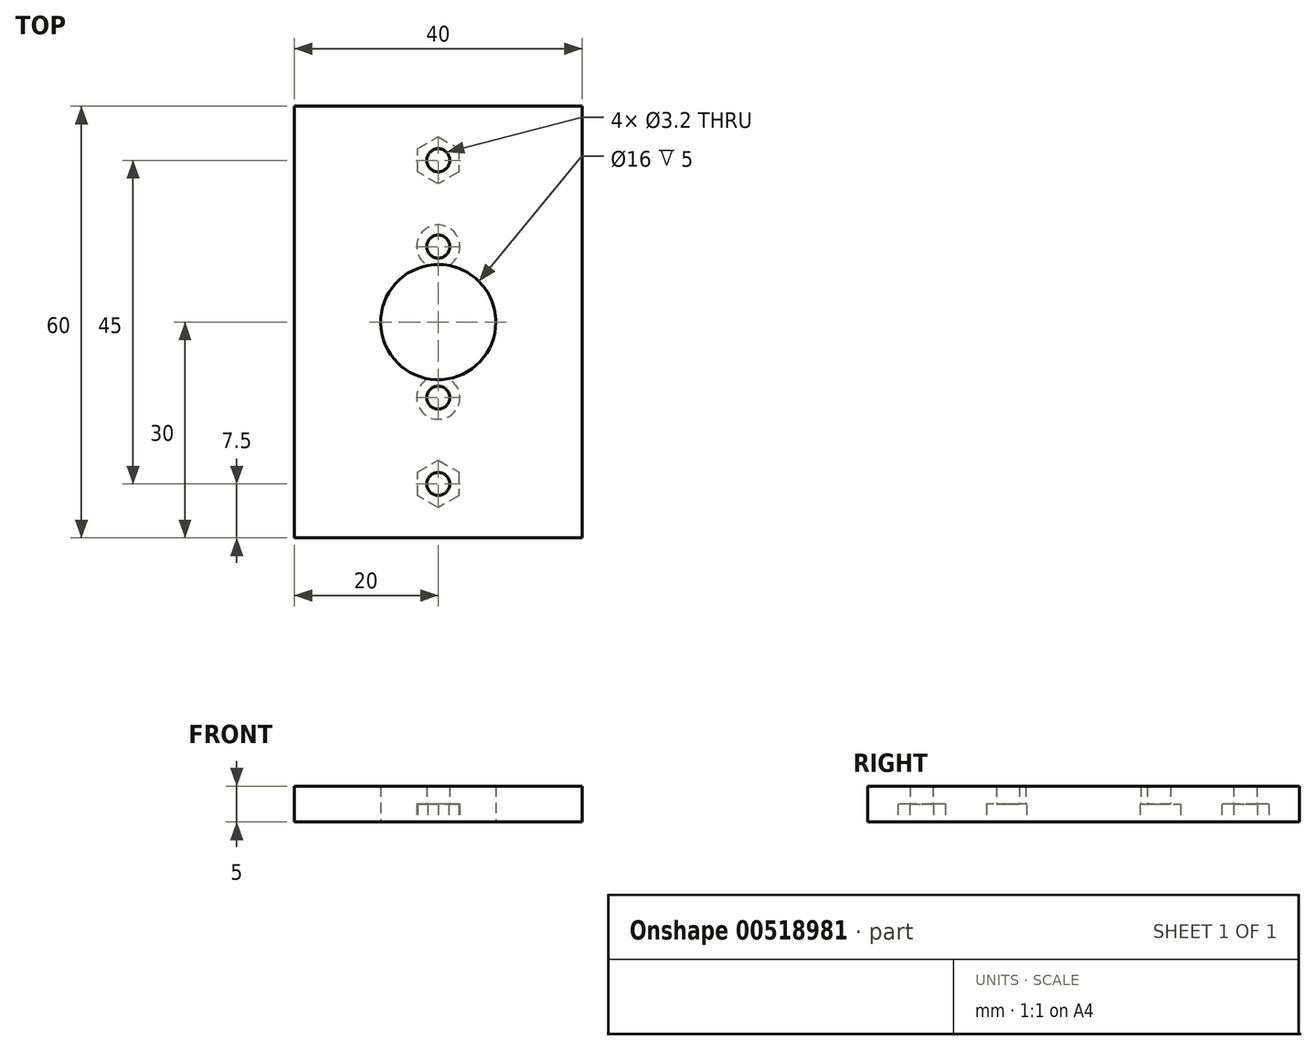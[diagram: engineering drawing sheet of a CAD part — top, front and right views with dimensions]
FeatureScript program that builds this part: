
annotation { "Feature Type Name" : "Feature", "Feature Type Description" : "" }
export const myFeature = defineFeature(function(context is Context, id is Id, definition is map)
    precondition{}
    {
        {
            var Q0;
            Q0=qCreatedBy(makeId("Top.planeOp"),FACE);
            var sketch = newSketch(context, id + "F0", { "sketchPlane" : qUnion([Q0])});
            skLineSegment(sketch, "E0.bottom", {"start": v(-20, 30) * mm, "end": v(20, 30) * mm});
            skLineSegment(sketch, "E0.top", {"start": v(-20, -30) * mm, "end": v(20, -30) * mm});
            skLineSegment(sketch, "E0.left", {"start": v(-20, 30) * mm, "end": v(-20, -30) * mm});
            skLineSegment(sketch, "E0.right", {"start": v(20, 30) * mm, "end": v(20, -30) * mm});
            skCircle(sketch, "E1.cCircle", {"center": v(0, 22.5) * mm, "radius": 2.85 * mm, "construction": true});
            skLineSegment(sketch, "E1.0", {"start": v(2.85, 20.85) * mm, "end": v(0, 19.2) * mm});
            skLineSegment(sketch, "E1.1", {"start": v(0, 19.2) * mm, "end": v(-2.85, 20.85) * mm});
            skLineSegment(sketch, "E1.2", {"start": v(-2.85, 20.85) * mm, "end": v(-2.85, 24.15) * mm});
            skLineSegment(sketch, "E1.3", {"start": v(-2.85, 24.15) * mm, "end": v(0, 25.8) * mm});
            skLineSegment(sketch, "E1.4", {"start": v(0, 25.8) * mm, "end": v(2.85, 24.15) * mm});
            skLineSegment(sketch, "E1.5", {"start": v(2.85, 24.15) * mm, "end": v(2.85, 20.85) * mm});
            skPoint(sketch, "E1.0.midPoint", {"position": v(1.43, 20.03) * mm});
            skCircle(sketch, "E2.cCircle", {"center": v(0, -22.5) * mm, "radius": 2.85 * mm, "construction": true});
            skLineSegment(sketch, "E2.0", {"start": v(2.85, -24.15) * mm, "end": v(0, -25.8) * mm});
            skLineSegment(sketch, "E2.1", {"start": v(0, -25.8) * mm, "end": v(-2.85, -24.15) * mm});
            skLineSegment(sketch, "E2.2", {"start": v(-2.85, -24.15) * mm, "end": v(-2.85, -20.85) * mm});
            skLineSegment(sketch, "E2.3", {"start": v(-2.85, -20.85) * mm, "end": v(0, -19.2) * mm});
            skLineSegment(sketch, "E2.4", {"start": v(0, -19.2) * mm, "end": v(2.85, -20.85) * mm});
            skLineSegment(sketch, "E2.5", {"start": v(2.85, -20.85) * mm, "end": v(2.85, -24.15) * mm});
            skPoint(sketch, "E2.0.midPoint", {"position": v(1.43, -24.97) * mm});
            skCircle(sketch, "E3", {"center": v(0, 22.5) * mm, "radius": 1.6 * mm});
            skCircle(sketch, "E4", {"center": v(0, -22.5) * mm, "radius": 1.6 * mm});
            skLineSegment(sketch, "E5", {"start": v(-20, 30) * mm, "end": v(20, -30) * mm, "construction": true});
            skCircle(sketch, "E6", {"center": v(0, 0) * mm, "radius": 8 * mm});
            skLineSegment(sketch, "E7", {"start": v(0, 22.5) * mm, "end": v(0, 0) * mm, "construction": true});
            skLineSegment(sketch, "E8", {"start": v(0, 0) * mm, "end": v(0, -22.5) * mm, "construction": true});
            skCircle(sketch, "E9", {"center": v(0, 10.5) * mm, "radius": 3 * mm});
            skCircle(sketch, "E10", {"center": v(0, -10.5) * mm, "radius": 3 * mm});
            skPoint(sketch, "E11", {"position": v(0, 11.25) * mm});
            skCircle(sketch, "E12", {"center": v(0, 10.5) * mm, "radius": 1.6 * mm});
            skCircle(sketch, "E13", {"center": v(0, -10.5) * mm, "radius": 1.6 * mm});
            skSolve(sketch);
        }
        {
            var Q0;
            Q0=makeQuery(id+"F0.imprint","IMPRINT",FACE,{"disambiguationData":[TD([[makeQuery(id+"F0.imprint","IMPRINT",EDGE,{"derivedFrom":sQuery(id+"F0.wireOp",EDGE,"E0.bottom")}),-1.0]])]});
            var Q1;
            Q1=makeQuery(id+"F0.imprint","IMPRINT",FACE,{"disambiguationData":[TD([[makeQuery(id+"F0.imprint","IMPRINT",EDGE,{"derivedFrom":sQuery(id+"F0.wireOp",EDGE,"E2.0")}),-1.0]])]});
            var Q2;
            Q2=makeQuery(id+"F0.imprint","IMPRINT",FACE,{"disambiguationData":[TD([[makeQuery(id+"F0.imprint","IMPRINT",EDGE,{"derivedFrom":sQuery(id+"F0.wireOp",EDGE,"E1.0")}),-1.0]])]});
            var Q3;
            Q3=makeQuery(id+"F0.imprint","IMPRINT",FACE,{"disambiguationData":[TD([[makeQuery(id+"F0.imprint","IMPRINT",EDGE,{"derivedFrom":sQuery(id+"F0.wireOp",EDGE,"E12")}),-1.0]])]});
            var Q4;
            Q4=makeQuery(id+"F0.imprint","IMPRINT",FACE,{"disambiguationData":[TD([[makeQuery(id+"F0.imprint","IMPRINT",EDGE,{"derivedFrom":sQuery(id+"F0.wireOp",EDGE,"E13")}),-1.0]])]});
            extrude(context, id + "F1", {"entities" : qUnion([Q0, Q1, Q2, Q3, Q4]), "depth" : 5 * mm, "offsetDistance" : 25 * mm});
        }
        {
            var Q0;
            Q0=makeQuery(id+"F0.imprint","IMPRINT",FACE,{"disambiguationData":[TD([[makeQuery(id+"F0.imprint","IMPRINT",EDGE,{"derivedFrom":sQuery(id+"F0.wireOp",EDGE,"E1.0")}),-1.0]])]});
            var Q1;
            Q1=makeQuery(id+"F0.imprint","IMPRINT",FACE,{"disambiguationData":[TD([[makeQuery(id+"F0.imprint","IMPRINT",EDGE,{"derivedFrom":sQuery(id+"F0.wireOp",EDGE,"E2.0")}),-1.0]])]});
            var Q2;
            Q2=makeQuery(id+"F0.imprint","IMPRINT",FACE,{"disambiguationData":[TD([[makeQuery(id+"F0.imprint","IMPRINT",EDGE,{"derivedFrom":sQuery(id+"F0.wireOp",EDGE,"E12")}),-1.0]])]});
            var Q3;
            Q3=makeQuery(id+"F0.imprint","IMPRINT",FACE,{"disambiguationData":[TD([[makeQuery(id+"F0.imprint","IMPRINT",EDGE,{"derivedFrom":sQuery(id+"F0.wireOp",EDGE,"E13")}),-1.0]])]});
            extrude(context, id + "F2", {"entities" : qUnion([Q0, Q1, Q2, Q3]), "operationType" : NewBodyOperationType.REMOVE, "depth" : 2.5 * mm, "offsetDistance" : 25 * mm});
        }
    });
